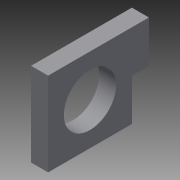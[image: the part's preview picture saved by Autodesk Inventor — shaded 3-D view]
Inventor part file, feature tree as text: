
AUTODESK INVENTOR PART (.ipt)
format: ipt  version: 2013 (Build 170138000, 138)  size: 88,064 bytes
history: native  units: mm
features: extrude x1, sketch x1
ambient origin geometry x8: Origin, YZ Plane, XZ Plane, XY Plane, X Axis, Y Axis, Z Axis, Center Point
feature tree (2):
  extrude  "Extrusion3"  Depth=3.0mm
  sketch  "Sketch1"  dims[d0=3.0mm d2=3.0mm d22=10.0mm d23=16.0mm d24=16.0mm d25=3.25mm d26=8.0mm d27=3.25mm d28=0.0mm]
